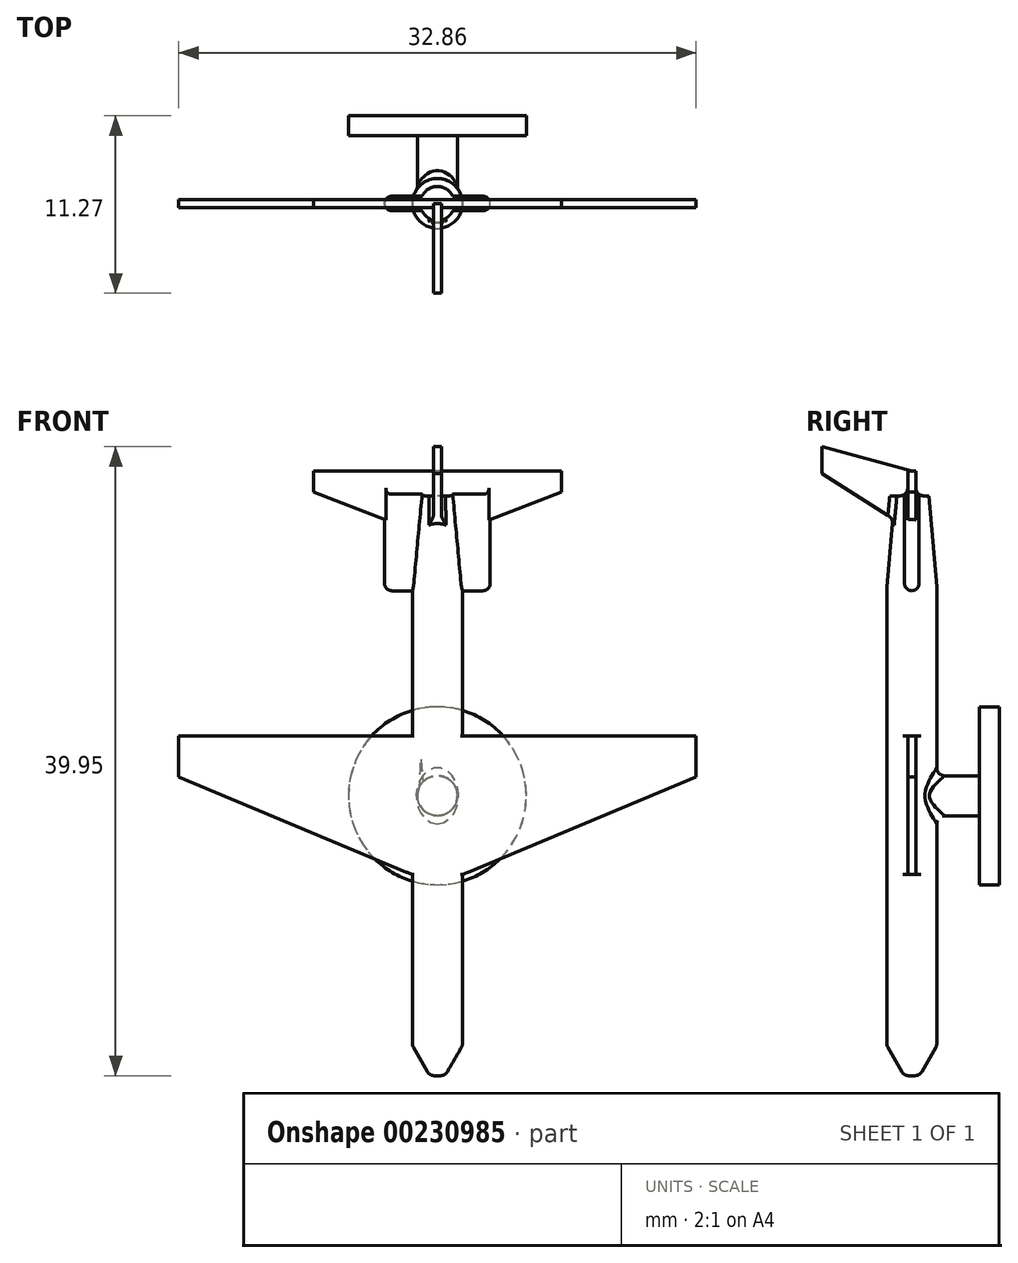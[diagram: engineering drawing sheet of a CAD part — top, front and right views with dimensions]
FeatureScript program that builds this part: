
annotation { "Feature Type Name" : "Feature", "Feature Type Description" : "" }
export const myFeature = defineFeature(function(context is Context, id is Id, definition is map)
    precondition{}
    {
        {
            var Q0;
            Q0=qCreatedBy(makeId("Top.planeOp"),FACE);
            var sketch = newSketch(context, id + "F0", { "sketchPlane" : qUnion([Q0])});
            skCircle(sketch, "E0", {"center": v(0, 0) * mm, "radius": 1.59 * mm});
            skSolve(sketch);
        }
        {
            var Q0;
            Q0 = qSketchRegion(id + "F0", true);
            extrude(context, id + "F1", {"entities" : qUnion([Q0]), "depth" : 36.83 * mm});
        }
        {
            var Q0;
            Q0=makeQuery(id+"F1.opExtrude","CAP_EDGE",EDGE,{"disambiguationData":[OSD([sQuery(id+"F0.wireOp",EDGE,"E0")])],"isStart":true});
            chamfer(context, id + "F2", {"entities" : qUnion([Q0]), "chamferType" : ChamferType.OFFSET_ANGLE, "width" : 1.9 * mm, "oppositeDirection" : false, "angle" : 30 * degree, "tangentPropagation" : true});
        }
        {
            var Q0;
            Q0=makeQuery(id+"F1.opExtrude","CAP_EDGE",EDGE,{"disambiguationData":[OSD([sQuery(id+"F0.wireOp",EDGE,"E0")])],"isStart":false});
            chamfer(context, id + "F3", {"entities" : qUnion([Q0]), "chamferType" : ChamferType.OFFSET_ANGLE, "width" : 0.5 * mm, "oppositeDirection" : false, "angle" : 85 * degree, "tangentPropagation" : true});
        }
        {
            var Q0;
            Q0=qCreatedBy(makeId("Front.planeOp"),FACE);
            var sketch = newSketch(context, id + "F4", { "sketchPlane" : qUnion([Q0])});
            skLineSegment(sketch, "E1", {"start": v(1.59, 31.02) * mm, "end": v(1.59, 1.9) * mm, "construction": true});
            skLineSegment(sketch, "E2", {"start": v(-1.59, 1.9) * mm, "end": v(-1.59, 31.02) * mm, "construction": true});
            skLineSegment(sketch, "E3", {"start": v(0, 36.83) * mm, "end": v(0, 0) * mm, "construction": true});
            skLineSegment(sketch, "E4", {"start": v(1.59, 12.77) * mm, "end": v(16.43, 18.97) * mm});
            skLineSegment(sketch, "E5", {"start": v(16.43, 18.97) * mm, "end": v(16.43, 21.58) * mm});
            skLineSegment(sketch, "E6", {"start": v(16.43, 21.58) * mm, "end": v(1.59, 21.58) * mm});
            skLineSegment(sketch, "E7.MirrorCS", {"start": v(-16.43, 21.58) * mm, "end": v(-1.59, 21.58) * mm});
            skLineSegment(sketch, "E8.MirrorCS", {"start": v(-16.43, 18.97) * mm, "end": v(-16.43, 21.58) * mm});
            skLineSegment(sketch, "E9.MirrorCS", {"start": v(-1.59, 12.77) * mm, "end": v(-16.43, 18.97) * mm});
            skLineSegment(sketch, "E10", {"start": v(1.59, 21.58) * mm, "end": v(-1.59, 21.58) * mm});
            skLineSegment(sketch, "E11", {"start": v(-1.59, 12.77) * mm, "end": v(1.59, 12.77) * mm});
            skLineSegment(sketch, "E12.0", {"start": v(-1.08, 36.83) * mm, "end": v(1.08, 36.83) * mm, "construction": true});
            skLineSegment(sketch, "E13", {"start": v(1.08, 36.83) * mm, "end": v(1.59, 31.02) * mm, "construction": true});
            skLineSegment(sketch, "E14", {"start": v(-1.59, 31.02) * mm, "end": v(-1.08, 36.83) * mm, "construction": true});
            skLineSegment(sketch, "E15", {"start": v(7.88, 38.4) * mm, "end": v(0, 38.4) * mm});
            skLineSegment(sketch, "E16.MirrorCS", {"start": v(-7.88, 38.4) * mm, "end": v(0, 38.4) * mm});
            skLineSegment(sketch, "E17", {"start": v(1.28, 34.54) * mm, "end": v(7.88, 37.07) * mm});
            skLineSegment(sketch, "E18", {"start": v(7.88, 37.07) * mm, "end": v(7.88, 38.4) * mm});
            skLineSegment(sketch, "E19.MirrorCS", {"start": v(-1.28, 34.54) * mm, "end": v(-7.88, 37.07) * mm});
            skLineSegment(sketch, "E20.MirrorCS", {"start": v(-7.88, 37.07) * mm, "end": v(-7.88, 38.4) * mm});
            skLineSegment(sketch, "E21", {"start": v(-1.28, 34.54) * mm, "end": v(1.28, 34.54) * mm});
            skSolve(sketch);
        }
        {
            var Q0;
            Q0 = qSketchRegion(id + "F4", true);
            extrude(context, id + "F5", {"entities" : qUnion([Q0]), "operationType" : NewBodyOperationType.ADD, "depth" : 0.25 * mm, "hasSecondDirection" : true, "secondDirectionOppositeDirection" : true, "secondDirectionDepth" : 0.25 * mm});
        }
        {
            var Q0;
            Q0=qCreatedBy(makeId("Front.planeOp"),FACE);
            var sketch = newSketch(context, id + "F6", { "sketchPlane" : qUnion([Q0])});
            skLineSegment(sketch, "E22", {"start": v(0, 27.6) * mm, "end": v(0, 41.25) * mm, "construction": true});
            skLineSegment(sketch, "E23", {"start": v(0, 30.8) * mm, "end": v(-3.35, 30.8) * mm});
            skLineSegment(sketch, "E24", {"start": v(-3.35, 30.8) * mm, "end": v(-3.35, 36.83) * mm});
            skLineSegment(sketch, "E25", {"start": v(-3.35, 36.83) * mm, "end": v(0, 36.83) * mm});
            skLineSegment(sketch, "E26.MirrorCS", {"start": v(3.35, 36.83) * mm, "end": v(0, 36.83) * mm});
            skLineSegment(sketch, "E27.MirrorCS", {"start": v(3.35, 30.8) * mm, "end": v(3.35, 36.83) * mm});
            skLineSegment(sketch, "E28.MirrorCS", {"start": v(0, 30.8) * mm, "end": v(3.35, 30.8) * mm});
            skSolve(sketch);
        }
        {
            var Q0;
            Q0 = qSketchRegion(id + "F6", true);
            extrude(context, id + "F7", {"entities" : qUnion([Q0]), "operationType" : NewBodyOperationType.ADD, "depth" : 0.46 * mm, "hasSecondDirection" : true, "secondDirectionOppositeDirection" : true, "secondDirectionDepth" : 0.46 * mm});
        }
        {
            var Q0;
            Q0=makeQuery(id+"F7.opExtrude","SWEPT_EDGE",EDGE,{"disambiguationData":[OSD([sQuery(id+"F6.wireOp",EDGE,"E27.MirrorCS"),sQuery(id+"F6.wireOp",EDGE,"E28.MirrorCS")])]});
            var Q1;
            Q1=makeQuery(id+"F7.opExtrude","CAP_EDGE",EDGE,{"disambiguationData":[OSD([sQuery(id+"F6.wireOp",EDGE,"E27.MirrorCS")])],"isStart":true});
            var Q2;
            Q2=makeQuery(id+"F7.opExtrude","CAP_EDGE",EDGE,{"disambiguationData":[OSD([sQuery(id+"F6.wireOp",EDGE,"E27.MirrorCS")])],"isStart":false});
            var Q3;
            Q3=makeQuery(id+"F7.opExtrude","CAP_EDGE",EDGE,{"disambiguationData":[OSD([sQuery(id+"F6.wireOp",EDGE,"E24")])],"isStart":true});
            var Q4;
            Q4=makeQuery(id+"F7.opExtrude","CAP_EDGE",EDGE,{"disambiguationData":[OSD([sQuery(id+"F6.wireOp",EDGE,"E24")])],"isStart":false});
            var Q5;
            Q5=makeQuery(id+"F7.opExtrude","SWEPT_EDGE",EDGE,{"disambiguationData":[OSD([sQuery(id+"F6.wireOp",EDGE,"E23"),sQuery(id+"F6.wireOp",EDGE,"E24")])]});
            var Q6;
            {var subQ0=sQuery(id+"F6.wireOp",EDGE,"E28.MirrorCS");var subQ1=sQuery(id+"F6.wireOp",EDGE,"E24");var subQ2=sQuery(id+"F6.wireOp",EDGE,"E23");Q6=makeQuery(id+"F7.boolean.opBoolean","SPLIT",EDGE,{"disambiguationData":[TD([makeQuery(id+"F7.opExtrude","SWEPT_FACE",FACE,{"disambiguationData":[OSD([subQ1])]})])],"derivedFrom":makeQuery(id+"F7.opExtrude","CAP_EDGE",EDGE,{"disambiguationData":[OSD([subQ2,subQ0])],"isStart":true})});}
            var Q7;
            {var subQ0=sQuery(id+"F6.wireOp",EDGE,"E28.MirrorCS");var subQ1=sQuery(id+"F6.wireOp",EDGE,"E27.MirrorCS");var subQ2=sQuery(id+"F6.wireOp",EDGE,"E23");Q7=makeQuery(id+"F7.boolean.opBoolean","SPLIT",EDGE,{"disambiguationData":[TD([makeQuery(id+"F7.opExtrude","SWEPT_FACE",FACE,{"disambiguationData":[OSD([subQ1])]})])],"derivedFrom":makeQuery(id+"F7.opExtrude","CAP_EDGE",EDGE,{"disambiguationData":[OSD([subQ2,subQ0])],"isStart":false})});}
            var Q8;
            {var subQ0=sQuery(id+"F6.wireOp",EDGE,"E28.MirrorCS");var subQ1=sQuery(id+"F6.wireOp",EDGE,"E27.MirrorCS");var subQ2=sQuery(id+"F6.wireOp",EDGE,"E23");Q8=makeQuery(id+"F7.boolean.opBoolean","SPLIT",EDGE,{"disambiguationData":[TD([makeQuery(id+"F7.opExtrude","SWEPT_FACE",FACE,{"disambiguationData":[OSD([subQ1])]})])],"derivedFrom":makeQuery(id+"F7.opExtrude","CAP_EDGE",EDGE,{"disambiguationData":[OSD([subQ2,subQ0])],"isStart":true})});}
            var Q9;
            {var subQ0=sQuery(id+"F6.wireOp",EDGE,"E28.MirrorCS");var subQ1=sQuery(id+"F6.wireOp",EDGE,"E24");var subQ2=sQuery(id+"F6.wireOp",EDGE,"E23");Q9=makeQuery(id+"F7.boolean.opBoolean","SPLIT",EDGE,{"disambiguationData":[TD([makeQuery(id+"F7.opExtrude","SWEPT_FACE",FACE,{"disambiguationData":[OSD([subQ1])]})])],"derivedFrom":makeQuery(id+"F7.opExtrude","CAP_EDGE",EDGE,{"disambiguationData":[OSD([subQ2,subQ0])],"isStart":false})});}
            fillet(context, id + "F8", {"entities" : qUnion([Q0, Q1, Q2, Q3, Q4, Q5, Q6, Q7, Q8, Q9]), "radius" : 0.46 * mm, "tangentPropagation" : true, "allowEdgeOverflow" : false});
        }
        {
            var Q0;
            Q0=qCreatedBy(makeId("Right.planeOp"),FACE);
            var sketch = newSketch(context, id + "F9", { "sketchPlane" : qUnion([Q0])});
            skLineSegment(sketch, "E29.0", {"start": v(-0.25, 38.4) * mm, "end": v(0.25, 38.4) * mm, "construction": true});
            skLineSegment(sketch, "E30", {"start": v(0, 38.4) * mm, "end": v(-5.7, 39.95) * mm});
            skLineSegment(sketch, "E31", {"start": v(-5.7, 39.95) * mm, "end": v(-5.7, 38.26) * mm});
            skLineSegment(sketch, "E32", {"start": v(-5.7, 38.26) * mm, "end": v(0, 34.6) * mm});
            skLineSegment(sketch, "E33", {"start": v(0, 38.4) * mm, "end": v(0, 34.6) * mm});
            skSolve(sketch);
        }
        {
            var Q0;
            Q0 = qSketchRegion(id + "F9", true);
            extrude(context, id + "F10", {"entities" : qUnion([Q0]), "operationType" : NewBodyOperationType.ADD, "depth" : 0.25 * mm, "hasSecondDirection" : true, "secondDirectionOppositeDirection" : true, "secondDirectionDepth" : 0.25 * mm});
        }
        {
            var Q0;
            Q0=qCreatedBy(makeId("Front.planeOp"),FACE);
            var sketch = newSketch(context, id + "F11", { "sketchPlane" : qUnion([Q0])});
            skCircle(sketch, "E34", {"center": v(0, 17.78) * mm, "radius": 1.27 * mm});
            skSolve(sketch);
        }
        {
            var Q0;
            Q0 = qSketchRegion(id + "F11", true);
            extrude(context, id + "F12", {"entities" : qUnion([Q0]), "operationType" : NewBodyOperationType.ADD, "oppositeDirection" : true, "depth" : 4.3 * mm});
        }
        {
            var Q0;
            Q0=makeQuery(id+"F12.opExtrude","CAP_FACE",FACE,{"disambiguationData":[OSD([sQuery(id+"F11.wireOp",EDGE,"E34")])],"isStart":false});
            var sketch = newSketch(context, id + "F13", { "sketchPlane" : qUnion([Q0])});
            skCircle(sketch, "E35", {"center": v(0, 17.78) * mm, "radius": 5.65 * mm});
            skSolve(sketch);
        }
        {
            var Q0;
            Q0 = qSketchRegion(id + "F13", true);
            extrude(context, id + "F14", {"entities" : qUnion([Q0]), "operationType" : NewBodyOperationType.ADD, "depth" : 1.27 * mm});
        }
        {
            var Q0;
            Q0=makeQuery(id+"F12.opExtrude","CAP_EDGE",EDGE,{"disambiguationData":[OSD([sQuery(id+"F11.wireOp",EDGE,"E34")])],"isStart":false});
            var Q1;
            Q1=makeQuery(id+"F5.boolean.opBoolean","INTERSECT",EDGE,{"disambiguationData":[OD(0.0)],"derivedFrom":[makeQuery(id+"F1.opExtrude","SWEPT_FACE",FACE,{"disambiguationData":[OSD([sQuery(id+"F0.wireOp",EDGE,"E0")])]}),makeQuery(id+"F5.opExtrude","CAP_FACE",FACE,{"disambiguationData":[OSD([sQuery(id+"F4.wireOp",EDGE,"E4"),sQuery(id+"F4.wireOp",EDGE,"E5"),sQuery(id+"F4.wireOp",EDGE,"E6"),sQuery(id+"F4.wireOp",EDGE,"E7.MirrorCS"),sQuery(id+"F4.wireOp",EDGE,"E8.MirrorCS"),sQuery(id+"F4.wireOp",EDGE,"E9.MirrorCS"),sQuery(id+"F4.wireOp",EDGE,"E10"),sQuery(id+"F4.wireOp",EDGE,"E11")])],"isStart":false})]});
            var Q2;
            {var subQ0=sQuery(id+"F0.wireOp",EDGE,"E0");Q2=makeQuery(id+"F2.opChamfer","BLEND_EDGE",EDGE,{"blendedFrom":[makeQuery(id+"F1.opExtrude","CAP_EDGE",EDGE,{"disambiguationData":[OSD([subQ0])],"isStart":true}),makeQuery(id+"F1.opExtrude","CAP_FACE",FACE,{"disambiguationData":[OSD([subQ0])],"isStart":true})],"blendedInto":[makeQuery(id+"F1.opExtrude","CAP_FACE",FACE,{"disambiguationData":[OSD([subQ0])],"isStart":true})]});}
            var Q3;
            Q3=makeQuery(id+"F12.boolean.opBoolean","INTERSECT",EDGE,{"derivedFrom":[makeQuery(id+"F1.opExtrude","SWEPT_FACE",FACE,{"disambiguationData":[OSD([sQuery(id+"F0.wireOp",EDGE,"E0")])]}),makeQuery(id+"F12.opExtrude","SWEPT_FACE",FACE,{"disambiguationData":[OSD([sQuery(id+"F11.wireOp",EDGE,"E34")])]})]});
            var Q4;
            {var subQ0=sQuery(id+"F0.wireOp",EDGE,"E0");var subQ1=makeQuery(id+"F1.opExtrude","SWEPT_FACE",FACE,{"disambiguationData":[OSD([subQ0])]});Q4=makeQuery(id+"F7.boolean.opBoolean","SPLIT",EDGE,{"disambiguationData":[TD([makeQuery(id+"F7.opExtrude","CAP_FACE",FACE,{"disambiguationData":[OSD([sQuery(id+"F6.wireOp",EDGE,"E23"),sQuery(id+"F6.wireOp",EDGE,"E24"),sQuery(id+"F6.wireOp",EDGE,"E25"),sQuery(id+"F6.wireOp",EDGE,"E26.MirrorCS"),sQuery(id+"F6.wireOp",EDGE,"E27.MirrorCS"),sQuery(id+"F6.wireOp",EDGE,"E28.MirrorCS")])],"isStart":true})])],"derivedFrom":makeQuery(id+"F3.opChamfer","BLEND_EDGE",EDGE,{"blendedFrom":[makeQuery(id+"F1.opExtrude","CAP_EDGE",EDGE,{"disambiguationData":[OSD([subQ0])],"isStart":false}),subQ1],"blendedInto":[subQ1]})});}
            var Q5;
            {var subQ0=sQuery(id+"F0.wireOp",EDGE,"E0");var subQ1=makeQuery(id+"F1.opExtrude","SWEPT_FACE",FACE,{"disambiguationData":[OSD([subQ0])]});Q5=makeQuery(id+"F7.boolean.opBoolean","SPLIT",EDGE,{"disambiguationData":[TD([makeQuery(id+"F7.opExtrude","CAP_FACE",FACE,{"disambiguationData":[OSD([sQuery(id+"F6.wireOp",EDGE,"E23"),sQuery(id+"F6.wireOp",EDGE,"E24"),sQuery(id+"F6.wireOp",EDGE,"E25"),sQuery(id+"F6.wireOp",EDGE,"E26.MirrorCS"),sQuery(id+"F6.wireOp",EDGE,"E27.MirrorCS"),sQuery(id+"F6.wireOp",EDGE,"E28.MirrorCS")])],"isStart":false})])],"derivedFrom":makeQuery(id+"F3.opChamfer","BLEND_EDGE",EDGE,{"blendedFrom":[makeQuery(id+"F1.opExtrude","CAP_EDGE",EDGE,{"disambiguationData":[OSD([subQ0])],"isStart":false}),subQ1],"blendedInto":[subQ1]})});}
            var Q6;
            Q6=makeQuery(id+"F7.boolean.opBoolean","INTERSECT",EDGE,{"derivedFrom":[makeQuery(id+"F5.opExtrude","CAP_FACE",FACE,{"disambiguationData":[OSD([sQuery(id+"F4.wireOp",EDGE,"E15"),sQuery(id+"F4.wireOp",EDGE,"E16.MirrorCS"),sQuery(id+"F4.wireOp",EDGE,"E17"),sQuery(id+"F4.wireOp",EDGE,"E18"),sQuery(id+"F4.wireOp",EDGE,"E19.MirrorCS"),sQuery(id+"F4.wireOp",EDGE,"E20.MirrorCS"),sQuery(id+"F4.wireOp",EDGE,"E21")])],"isStart":true}),makeQuery(id+"F7.opExtrude","SWEPT_FACE",FACE,{"disambiguationData":[OSD([sQuery(id+"F6.wireOp",EDGE,"E25"),sQuery(id+"F6.wireOp",EDGE,"E26.MirrorCS")])]})]});
            var Q7;
            Q7=makeQuery(id+"F7.boolean.opBoolean","INTERSECT",EDGE,{"derivedFrom":[makeQuery(id+"F5.opExtrude","CAP_FACE",FACE,{"disambiguationData":[OSD([sQuery(id+"F4.wireOp",EDGE,"E15"),sQuery(id+"F4.wireOp",EDGE,"E16.MirrorCS"),sQuery(id+"F4.wireOp",EDGE,"E17"),sQuery(id+"F4.wireOp",EDGE,"E18"),sQuery(id+"F4.wireOp",EDGE,"E19.MirrorCS"),sQuery(id+"F4.wireOp",EDGE,"E20.MirrorCS"),sQuery(id+"F4.wireOp",EDGE,"E21")])],"isStart":false}),makeQuery(id+"F7.opExtrude","SWEPT_FACE",FACE,{"disambiguationData":[OSD([sQuery(id+"F6.wireOp",EDGE,"E25"),sQuery(id+"F6.wireOp",EDGE,"E26.MirrorCS")])]})]});
            var Q8;
            Q8=makeQuery(id+"F5.boolean.opBoolean","INTERSECT",EDGE,{"disambiguationData":[OD(1.0)],"derivedFrom":[makeQuery(id+"F1.opExtrude","SWEPT_FACE",FACE,{"disambiguationData":[OSD([sQuery(id+"F0.wireOp",EDGE,"E0")])]}),makeQuery(id+"F5.opExtrude","CAP_FACE",FACE,{"disambiguationData":[OSD([sQuery(id+"F4.wireOp",EDGE,"E4"),sQuery(id+"F4.wireOp",EDGE,"E5"),sQuery(id+"F4.wireOp",EDGE,"E6"),sQuery(id+"F4.wireOp",EDGE,"E7.MirrorCS"),sQuery(id+"F4.wireOp",EDGE,"E8.MirrorCS"),sQuery(id+"F4.wireOp",EDGE,"E9.MirrorCS"),sQuery(id+"F4.wireOp",EDGE,"E10"),sQuery(id+"F4.wireOp",EDGE,"E11")])],"isStart":false})]});
            var Q9;
            Q9=makeQuery(id+"F5.boolean.opBoolean","INTERSECT",EDGE,{"disambiguationData":[OD(1.0)],"derivedFrom":[makeQuery(id+"F1.opExtrude","SWEPT_FACE",FACE,{"disambiguationData":[OSD([sQuery(id+"F0.wireOp",EDGE,"E0")])]}),makeQuery(id+"F5.opExtrude","CAP_FACE",FACE,{"disambiguationData":[OSD([sQuery(id+"F4.wireOp",EDGE,"E4"),sQuery(id+"F4.wireOp",EDGE,"E5"),sQuery(id+"F4.wireOp",EDGE,"E6"),sQuery(id+"F4.wireOp",EDGE,"E7.MirrorCS"),sQuery(id+"F4.wireOp",EDGE,"E8.MirrorCS"),sQuery(id+"F4.wireOp",EDGE,"E9.MirrorCS"),sQuery(id+"F4.wireOp",EDGE,"E10"),sQuery(id+"F4.wireOp",EDGE,"E11")])],"isStart":true})]});
            var Q10;
            Q10=makeQuery(id+"F5.boolean.opBoolean","INTERSECT",EDGE,{"disambiguationData":[OD(0.0)],"derivedFrom":[makeQuery(id+"F1.opExtrude","SWEPT_FACE",FACE,{"disambiguationData":[OSD([sQuery(id+"F0.wireOp",EDGE,"E0")])]}),makeQuery(id+"F5.opExtrude","CAP_FACE",FACE,{"disambiguationData":[OSD([sQuery(id+"F4.wireOp",EDGE,"E4"),sQuery(id+"F4.wireOp",EDGE,"E5"),sQuery(id+"F4.wireOp",EDGE,"E6"),sQuery(id+"F4.wireOp",EDGE,"E7.MirrorCS"),sQuery(id+"F4.wireOp",EDGE,"E8.MirrorCS"),sQuery(id+"F4.wireOp",EDGE,"E9.MirrorCS"),sQuery(id+"F4.wireOp",EDGE,"E10"),sQuery(id+"F4.wireOp",EDGE,"E11")])],"isStart":true})]});
            var Q11;
            {var subQ0=sQuery(id+"F0.wireOp",EDGE,"E0");Q11=makeQuery(id+"F2.opChamfer","BLEND_EDGE",EDGE,{"blendedFrom":[makeQuery(id+"F1.opExtrude","CAP_EDGE",EDGE,{"disambiguationData":[OSD([subQ0])],"isStart":true}),makeQuery(id+"F1.opExtrude","SWEPT_FACE",FACE,{"disambiguationData":[OSD([subQ0])]})],"blendedInto":[makeQuery(id+"F1.opExtrude","SWEPT_FACE",FACE,{"disambiguationData":[OSD([subQ0])]})]});}
            var Q12;
            {var subQ0=sQuery(id+"F0.wireOp",EDGE,"E0");var subQ1=sQuery(id+"F6.wireOp",EDGE,"E26.MirrorCS");var subQ2=sQuery(id+"F6.wireOp",EDGE,"E25");Q12=makeQuery(id+"F10.boolean.opBoolean","INTERSECT",EDGE,{"derivedFrom":[makeQuery(id+"F7.boolean.opBoolean","SPLIT",FACE,{"disambiguationData":[TD([makeQuery(id+"F7.opExtrude","CAP_FACE",FACE,{"disambiguationData":[OSD([sQuery(id+"F6.wireOp",EDGE,"E23"),sQuery(id+"F6.wireOp",EDGE,"E24"),subQ2,subQ1,sQuery(id+"F6.wireOp",EDGE,"E27.MirrorCS"),sQuery(id+"F6.wireOp",EDGE,"E28.MirrorCS")])],"isStart":false})])],"derivedFrom":makeQuery(id+"F3.opChamfer","BLEND_FACE",FACE,{"disambiguationData":[OSD([subQ0])]})}),makeQuery(id+"F10.opExtrude","CAP_FACE",FACE,{"disambiguationData":[OSD([sQuery(id+"F9.wireOp",EDGE,"E30"),sQuery(id+"F9.wireOp",EDGE,"E31"),sQuery(id+"F9.wireOp",EDGE,"E32"),sQuery(id+"F9.wireOp",EDGE,"E33")])],"isStart":true})]});}
            var Q13;
            {var subQ0=sQuery(id+"F0.wireOp",EDGE,"E0");var subQ1=sQuery(id+"F6.wireOp",EDGE,"E26.MirrorCS");var subQ2=sQuery(id+"F6.wireOp",EDGE,"E25");Q13=makeQuery(id+"F10.boolean.opBoolean","INTERSECT",EDGE,{"derivedFrom":[makeQuery(id+"F7.boolean.opBoolean","SPLIT",FACE,{"disambiguationData":[TD([makeQuery(id+"F7.opExtrude","CAP_FACE",FACE,{"disambiguationData":[OSD([sQuery(id+"F6.wireOp",EDGE,"E23"),sQuery(id+"F6.wireOp",EDGE,"E24"),subQ2,subQ1,sQuery(id+"F6.wireOp",EDGE,"E27.MirrorCS"),sQuery(id+"F6.wireOp",EDGE,"E28.MirrorCS")])],"isStart":false})])],"derivedFrom":makeQuery(id+"F3.opChamfer","BLEND_FACE",FACE,{"disambiguationData":[OSD([subQ0])]})}),makeQuery(id+"F10.opExtrude","CAP_FACE",FACE,{"disambiguationData":[OSD([sQuery(id+"F9.wireOp",EDGE,"E30"),sQuery(id+"F9.wireOp",EDGE,"E31"),sQuery(id+"F9.wireOp",EDGE,"E32"),sQuery(id+"F9.wireOp",EDGE,"E33")])],"isStart":false})]});}
            var Q14;
            {var subQ0=sQuery(id+"F0.wireOp",EDGE,"E0");var subQ1=sQuery(id+"F6.wireOp",EDGE,"E26.MirrorCS");var subQ2=sQuery(id+"F6.wireOp",EDGE,"E25");Q14=makeQuery(id+"F10.boolean.opBoolean","INTERSECT",EDGE,{"derivedFrom":[makeQuery(id+"F7.boolean.opBoolean","SPLIT",FACE,{"disambiguationData":[TD([makeQuery(id+"F7.opExtrude","CAP_FACE",FACE,{"disambiguationData":[OSD([sQuery(id+"F6.wireOp",EDGE,"E23"),sQuery(id+"F6.wireOp",EDGE,"E24"),subQ2,subQ1,sQuery(id+"F6.wireOp",EDGE,"E27.MirrorCS"),sQuery(id+"F6.wireOp",EDGE,"E28.MirrorCS")])],"isStart":false})])],"derivedFrom":makeQuery(id+"F3.opChamfer","BLEND_FACE",FACE,{"disambiguationData":[OSD([subQ0])]})}),makeQuery(id+"F10.opExtrude","SWEPT_FACE",FACE,{"disambiguationData":[OSD([sQuery(id+"F9.wireOp",EDGE,"E32")])]})]});}
            fillet(context, id + "F15", {"entities" : qUnion([Q0, Q1, Q2, Q3, Q4, Q5, Q6, Q7, Q8, Q9, Q10, Q11, Q12, Q13, Q14]), "radius" : 0.5 * mm, "tangentPropagation" : true, "allowEdgeOverflow" : false});
        }
    });
